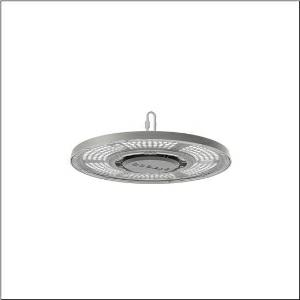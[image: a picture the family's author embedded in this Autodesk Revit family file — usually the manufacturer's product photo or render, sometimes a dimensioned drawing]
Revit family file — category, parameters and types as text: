
# Revit family: highbay_31-s_51hc41da4fmb
name_source: partatom
category: Lighting Fixtures
units: mm (PartAtom-declared; Revit-internal decimal feet)

## family parameters
Cut with Voids When Loaded = No
Host = Face
Light Source = No
Part Type = Normal
Room Calculation Point = No
Round Connector Dimension = Use Diameter
Shared = No

## types (1)
- Highbay 31-S (1 x LED, 14000 lm, 94 W, 4000K)
    Apparent Load = 94 VA
    CIE Flux Codes = 94 98 100 100 100
    Color Rendering = 80
    Color Temperature = 4000K
    Default Elevation = 1800 mm
    Description = Highbay 31-S, LED high bay luminaire, primary light control with lens, of PC, primary optical cover: cover panel, of PC, transparent, light emission: direct distribution, primary light characteristic: rotationally symmetric, installation type: suspended mounting, surface-mounted, LED, rated luminous flux: 14.000lm, luminous efficacy: 150lm/W, light colour: 840, colour temperature: 4000K, control gear: ECG DALI, with cable, 5x 1.0mm², free wire ends, mains connection: 220..240V, AC/DC, 0/50..60Hz, cable length: 1,5m, rated input power: 94W, housing, rotationally symmetric, of diecast aluminium, grey aluminium (RAL 9007), diameter: 339mm, protection rating (complete): IP65, insulation class (complete): insulation class I (protective earthing), certification: CE, ENEC, UKCA, protection symbol: D, impact resistance: IK08, permissible operating ambient temperature: -30..+45°C, standard: EN 60598-2-22, EN 60598, corresponds to IFS (International Featured Standards) requirements for safety and quality in the food industry, packaging unit: 1 piece
    Height = 141 mm
    Lamp = 1 x LED
    Lamp Light Flux = 14000 lm
    Lamp Power = 94 W
    Lamp count = 1
    Length = 339 mm
    Luminous efficacy = 149 lm/W
    Manufacturer = Siteco
    ModVariant = No
    Model = 51HC41DA4FMB
    Mounting Place = Ceiling
    Mounting Type = Pendant
    Number of Poles = 1
    OnlyDefault = Yes
    Power Factor = 1
    Product Name = Highbay 31-S
    Product group = LED high bay luminaire
    ProductGroupID = 903
    Protection Class = Protection class I
    Protection Degree = IP 65
    RLX_Detail_Level = 1
    RlxData = <blob elided: 107453 chars, md5=510b0848>
    Socket = socket
    Standby Power = 0 W
    System Light Flux = 14000 lm
    System Power = 94 W
    Type Comments = Product without accessories
    Type Image = l_1007237.jpg
    URL = http://relux.com
    VarID = ---
    Voltage = 0 V
    Weight = 0.00 kg
    Width = 0 mm  [stored 0 ft]

note: [stored X ft] marks values corroborated as IEEE doubles in the binary element streams (Revit-internal decimal feet)

## geometry (parser evidence)
native form markers: Blend x4, Sweep x10
no freeform markers — native parametric forms only
